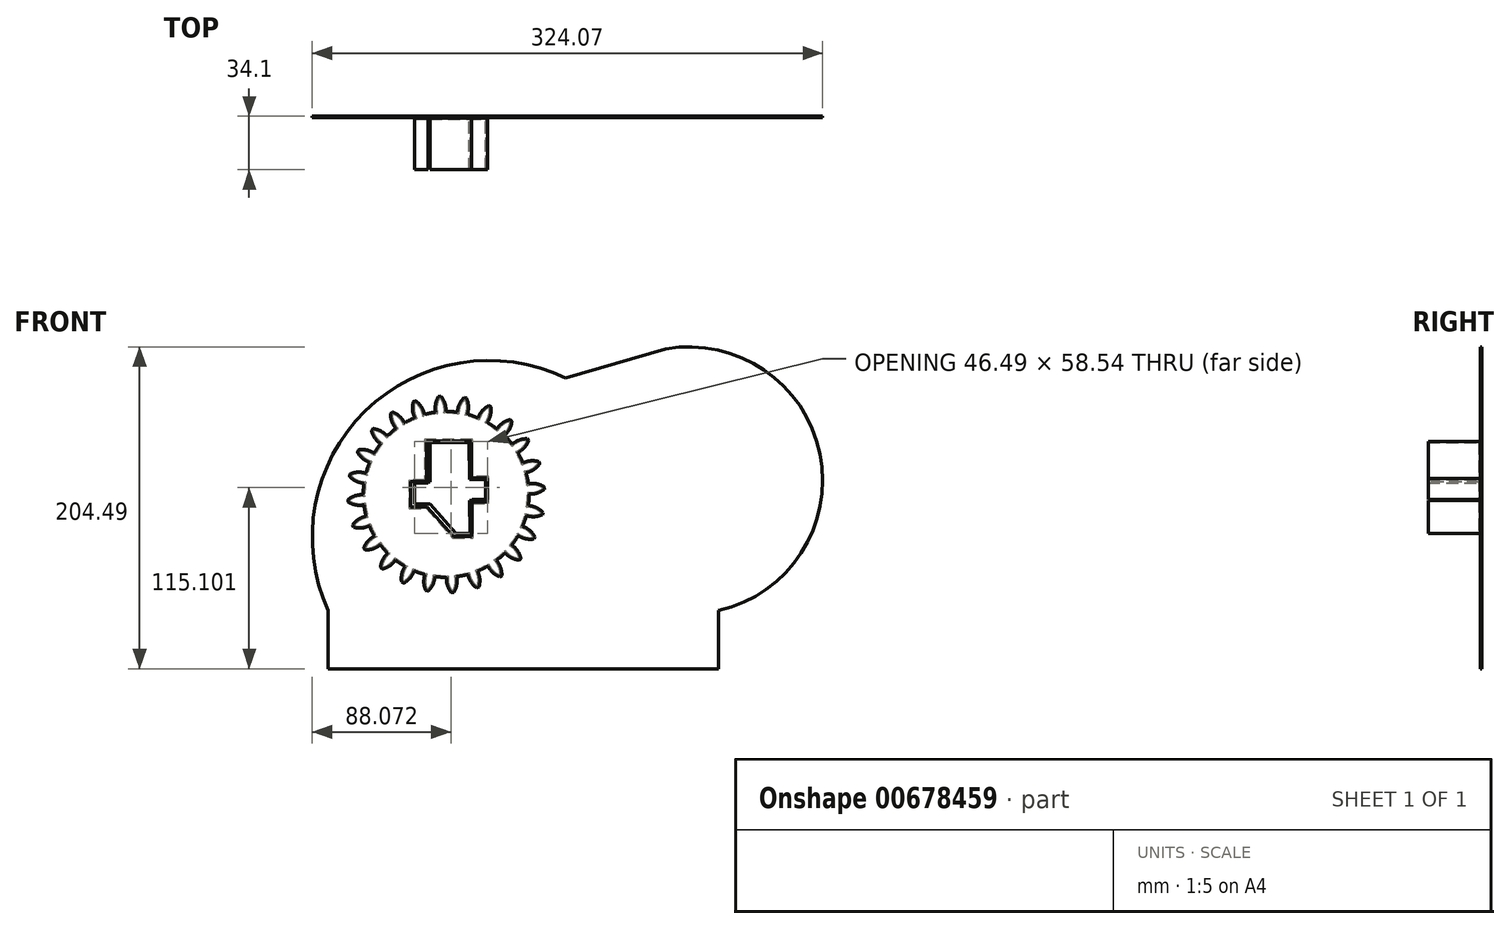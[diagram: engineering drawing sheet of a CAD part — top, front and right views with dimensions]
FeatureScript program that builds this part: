
annotation { "Feature Type Name" : "Feature", "Feature Type Description" : "" }
export const myFeature = defineFeature(function(context is Context, id is Id, definition is map)
    precondition{}
    {
        {
            var Q0;
            Q0=qCreatedBy(makeId("Front.planeOp"),FACE);
            var sketch = newSketch(context, id + "F0", { "sketchPlane" : qUnion([Q0])});
            skCircle(sketch, "E0", {"center": v(0, 0) * mm, "radius": 53.72 * mm});
            skCircle(sketch, "E1", {"center": v(0, 0) * mm, "radius": 63.5 * mm, "construction": true});
            skCircle(sketch, "E2", {"center": v(0, 0) * mm, "radius": 58.67 * mm, "construction": true});
            skLineSegment(sketch, "E3", {"start": v(0, 0) * mm, "end": v(0, 121.01) * mm, "construction": true});
            skLineSegment(sketch, "E4", {"start": v(0, 0) * mm, "end": v(-7.93, 121.01) * mm, "construction": true});
            skLineSegment(sketch, "E5", {"start": v(0, 58.67) * mm, "end": v(-96.86, 58.67) * mm, "construction": true});
            skLineSegment(sketch, "E6", {"start": v(0, 58.67) * mm, "end": v(-98.4, 22.86) * mm, "construction": true});
            skCircle(sketch, "E7", {"center": v(0, 0) * mm, "radius": 55.14 * mm, "construction": true});
            skCircle(sketch, "E8", {"center": v(0, 58.67) * mm, "radius": 14.6 * mm, "construction": true});
            skCircle(sketch, "E9", {"center": v(-13.72, 53.68) * mm, "radius": 14.6 * mm, "construction": true});
            skArc(sketch, "E10", {"start": v(0, 58.67) * mm, "mid": v(-1.21, 61.19) * mm, "end": v(-2.86, 63.44) * mm});
            skArc(sketch, "E11", {"start": v(0.8, 55.13) * mm, "mid": v(0.5, 56.92) * mm, "end": v(0, 58.67) * mm});
            skArc(sketch, "E12", {"start": v(0.88, 53.71) * mm, "mid": v(0.64, 56.23) * mm, "end": v(0, 58.67) * mm});
            skArc(sketch, "E13.MirrorCS", {"start": v(-7.88, 53.14) * mm, "mid": v(-7.98, 55.66) * mm, "end": v(-7.66, 58.17) * mm});
            skArc(sketch, "E14.MirrorCS", {"start": v(-7.66, 58.17) * mm, "mid": v(-6.79, 60.82) * mm, "end": v(-5.45, 63.27) * mm});
            skLineSegment(sketch, "E15", {"start": v(-5.45, 63.27) * mm, "end": v(-2.86, 63.44) * mm});
            skLineSegment(sketch, "E16", {"start": v(-11.56, -6.88) * mm, "end": v(-21.56, -6.88) * mm});
            skLineSegment(sketch, "E17", {"start": v(-21.56, -6.88) * mm, "end": v(-21.56, 7.27) * mm});
            skLineSegment(sketch, "E18", {"start": v(-21.56, 7.27) * mm, "end": v(-11.56, 7.27) * mm});
            skLineSegment(sketch, "E19", {"start": v(-11.56, 7.27) * mm, "end": v(-11.56, 32.9) * mm});
            skLineSegment(sketch, "E20", {"start": v(-11.56, 32.9) * mm, "end": v(14.67, 32.9) * mm});
            skLineSegment(sketch, "E21", {"start": v(14.67, 32.9) * mm, "end": v(14.72, 9.39) * mm});
            skLineSegment(sketch, "E22", {"start": v(14.72, 9.39) * mm, "end": v(24.9, 9.41) * mm});
            skLineSegment(sketch, "E23", {"start": v(24.9, 9.41) * mm, "end": v(24.93, -3.87) * mm});
            skLineSegment(sketch, "E24", {"start": v(24.93, -3.87) * mm, "end": v(14.93, -3.9) * mm});
            skLineSegment(sketch, "E25", {"start": v(14.93, -3.9) * mm, "end": v(15.04, -25.59) * mm});
            skLineSegment(sketch, "E26", {"start": v(15.04, -25.59) * mm, "end": v(5.04, -25.64) * mm});
            skLineSegment(sketch, "E27", {"start": v(5.04, -25.64) * mm, "end": v(-11.56, -6.88) * mm});
            skCircle(sketch, "E28", {"center": v(0, 0) * mm, "radius": 43.91 * mm});
            skSolve(sketch);
        }
        {
            var Q0;
            Q0=makeQuery(id+"F0.imprint","IMPRINT",FACE,{"disambiguationData":[TD([[makeQuery(id+"F0.imprint","IMPRINT",EDGE,{"derivedFrom":sQuery(id+"F0.wireOp",EDGE,"E28")}),-1.0]])]});
            var Q1;
            {var subQ5=sQuery(id+"F0.wireOp",EDGE,"E10");Q1=makeQuery(id+"F0.imprint","IMPRINT",FACE,{"disambiguationData":[TD([[makeQuery(id+"F0.imprint","IMPRINT",EDGE,{"derivedFrom":subQ5}),1.0]])]});}
            extrude(context, id + "F1", {"entities" : qUnion([Q0, Q1]), "depth" : 25 * mm, "offsetDistance" : 25 * mm});
        }
        {
            var Q0;
            Q0=makeQuery(id+"F1.opExtrude","SWEPT_BODY",BODY,{"disambiguationData":[OSD([sQuery(id+"F0.wireOp",EDGE,"E0"),sQuery(id+"F0.wireOp",EDGE,"E10"),sQuery(id+"F0.wireOp",EDGE,"E12"),sQuery(id+"F0.wireOp",EDGE,"E13.MirrorCS"),sQuery(id+"F0.wireOp",EDGE,"E14.MirrorCS"),sQuery(id+"F0.wireOp",EDGE,"E15")])]});
            var Q1;
            Q1=makeQuery(id+"F1.opExtrude","SWEPT_FACE",FACE,{"disambiguationData":[OSD([sQuery(id+"F0.wireOp",EDGE,"E0")])]});
            circularPattern(context, id + "F2", {"entities" : qUnion([Q0]), "axis" : qUnion([Q1]), "angle" : 360 * degree, "instanceCount" : 24, "equalSpace" : true});
        }
        {
            var Q0;
            Q0=makeQuery(id+"F0.imprint","IMPRINT",FACE,{"disambiguationData":[TD([[makeQuery(id+"F0.imprint","IMPRINT",EDGE,{"derivedFrom":sQuery(id+"F0.wireOp",EDGE,"E16")}),1.0]])]});
            extrude(context, id + "F3", {"entities" : qUnion([Q0]), "operationType" : NewBodyOperationType.ADD, "depth" : 34.1 * mm, "offsetDistance" : 25 * mm});
        }
        {
            var Q0;
            {var subQ0=sQuery(id+"F0.wireOp",EDGE,"E28");var subQ1=makeQuery(id+"F1.opExtrude","CAP_FACE",FACE,{"disambiguationData":[OSD([sQuery(id+"F0.wireOp",EDGE,"E0"),sQuery(id+"F0.wireOp",EDGE,"E10"),sQuery(id+"F0.wireOp",EDGE,"E11"),sQuery(id+"F0.wireOp",EDGE,"E12"),sQuery(id+"F0.wireOp",EDGE,"E13.MirrorCS"),sQuery(id+"F0.wireOp",EDGE,"E14.MirrorCS"),sQuery(id+"F0.wireOp",EDGE,"E15"),subQ0])],"isStart":true});Q0=makeQuery(id+"F3.boolean.opBoolean","MERGE",FACE,{"derivedFrom":[subQ1,makeQuery(id+"F2.opPattern","COPY",FACE,{"derivedFrom":subQ1,"instanceName":"1"}),makeQuery(id+"F2.opPattern","COPY",FACE,{"derivedFrom":subQ1,"instanceName":"2"}),makeQuery(id+"F2.opPattern","COPY",FACE,{"derivedFrom":subQ1,"instanceName":"3"}),makeQuery(id+"F2.opPattern","COPY",FACE,{"derivedFrom":subQ1,"instanceName":"4"}),makeQuery(id+"F2.opPattern","COPY",FACE,{"derivedFrom":subQ1,"instanceName":"5"}),makeQuery(id+"F2.opPattern","COPY",FACE,{"derivedFrom":subQ1,"instanceName":"6"}),makeQuery(id+"F2.opPattern","COPY",FACE,{"derivedFrom":subQ1,"instanceName":"7"}),makeQuery(id+"F2.opPattern","COPY",FACE,{"derivedFrom":subQ1,"instanceName":"8"}),makeQuery(id+"F2.opPattern","COPY",FACE,{"derivedFrom":subQ1,"instanceName":"9"}),makeQuery(id+"F2.opPattern","COPY",FACE,{"derivedFrom":subQ1,"instanceName":"10"}),makeQuery(id+"F2.opPattern","COPY",FACE,{"derivedFrom":subQ1,"instanceName":"11"}),makeQuery(id+"F2.opPattern","COPY",FACE,{"derivedFrom":subQ1,"instanceName":"12"}),makeQuery(id+"F2.opPattern","COPY",FACE,{"derivedFrom":subQ1,"instanceName":"13"}),makeQuery(id+"F2.opPattern","COPY",FACE,{"derivedFrom":subQ1,"instanceName":"14"}),makeQuery(id+"F2.opPattern","COPY",FACE,{"derivedFrom":subQ1,"instanceName":"15"}),makeQuery(id+"F2.opPattern","COPY",FACE,{"derivedFrom":subQ1,"instanceName":"16"}),makeQuery(id+"F2.opPattern","COPY",FACE,{"derivedFrom":subQ1,"instanceName":"17"}),makeQuery(id+"F2.opPattern","COPY",FACE,{"derivedFrom":subQ1,"instanceName":"18"}),makeQuery(id+"F2.opPattern","COPY",FACE,{"derivedFrom":subQ1,"instanceName":"19"}),makeQuery(id+"F2.opPattern","COPY",FACE,{"derivedFrom":subQ1,"instanceName":"20"}),makeQuery(id+"F2.opPattern","COPY",FACE,{"derivedFrom":subQ1,"instanceName":"21"}),makeQuery(id+"F2.opPattern","COPY",FACE,{"derivedFrom":subQ1,"instanceName":"22"}),makeQuery(id+"F2.opPattern","COPY",FACE,{"derivedFrom":subQ1,"instanceName":"23"}),makeQuery(id+"F3.opExtrude","CAP_FACE",FACE,{"disambiguationData":[OSD([sQuery(id+"F0.wireOp",EDGE,"E16"),sQuery(id+"F0.wireOp",EDGE,"E17"),sQuery(id+"F0.wireOp",EDGE,"E18"),sQuery(id+"F0.wireOp",EDGE,"E19"),sQuery(id+"F0.wireOp",EDGE,"E20"),sQuery(id+"F0.wireOp",EDGE,"E21"),sQuery(id+"F0.wireOp",EDGE,"E22"),sQuery(id+"F0.wireOp",EDGE,"E23"),sQuery(id+"F0.wireOp",EDGE,"E24"),sQuery(id+"F0.wireOp",EDGE,"E25"),sQuery(id+"F0.wireOp",EDGE,"E26"),sQuery(id+"F0.wireOp",EDGE,"E27"),subQ0])],"isStart":true})]});}
            var Q1;
            {var subQ0=makeQuery(id+"F1.opExtrude","CAP_FACE",FACE,{"disambiguationData":[OSD([sQuery(id+"F0.wireOp",EDGE,"E0"),sQuery(id+"F0.wireOp",EDGE,"E10"),sQuery(id+"F0.wireOp",EDGE,"E11"),sQuery(id+"F0.wireOp",EDGE,"E12"),sQuery(id+"F0.wireOp",EDGE,"E13.MirrorCS"),sQuery(id+"F0.wireOp",EDGE,"E14.MirrorCS"),sQuery(id+"F0.wireOp",EDGE,"E15"),sQuery(id+"F0.wireOp",EDGE,"E28")])],"isStart":false});Q1=makeQuery(id+"F3.boolean.opBoolean","MERGE",FACE,{"derivedFrom":[subQ0,makeQuery(id+"F2.opPattern","COPY",FACE,{"derivedFrom":subQ0,"instanceName":"1"}),makeQuery(id+"F2.opPattern","COPY",FACE,{"derivedFrom":subQ0,"instanceName":"2"}),makeQuery(id+"F2.opPattern","COPY",FACE,{"derivedFrom":subQ0,"instanceName":"3"}),makeQuery(id+"F2.opPattern","COPY",FACE,{"derivedFrom":subQ0,"instanceName":"4"}),makeQuery(id+"F2.opPattern","COPY",FACE,{"derivedFrom":subQ0,"instanceName":"5"}),makeQuery(id+"F2.opPattern","COPY",FACE,{"derivedFrom":subQ0,"instanceName":"6"}),makeQuery(id+"F2.opPattern","COPY",FACE,{"derivedFrom":subQ0,"instanceName":"7"}),makeQuery(id+"F2.opPattern","COPY",FACE,{"derivedFrom":subQ0,"instanceName":"8"}),makeQuery(id+"F2.opPattern","COPY",FACE,{"derivedFrom":subQ0,"instanceName":"9"}),makeQuery(id+"F2.opPattern","COPY",FACE,{"derivedFrom":subQ0,"instanceName":"10"}),makeQuery(id+"F2.opPattern","COPY",FACE,{"derivedFrom":subQ0,"instanceName":"11"}),makeQuery(id+"F2.opPattern","COPY",FACE,{"derivedFrom":subQ0,"instanceName":"12"}),makeQuery(id+"F2.opPattern","COPY",FACE,{"derivedFrom":subQ0,"instanceName":"13"}),makeQuery(id+"F2.opPattern","COPY",FACE,{"derivedFrom":subQ0,"instanceName":"14"}),makeQuery(id+"F2.opPattern","COPY",FACE,{"derivedFrom":subQ0,"instanceName":"15"}),makeQuery(id+"F2.opPattern","COPY",FACE,{"derivedFrom":subQ0,"instanceName":"16"}),makeQuery(id+"F2.opPattern","COPY",FACE,{"derivedFrom":subQ0,"instanceName":"17"}),makeQuery(id+"F2.opPattern","COPY",FACE,{"derivedFrom":subQ0,"instanceName":"18"}),makeQuery(id+"F2.opPattern","COPY",FACE,{"derivedFrom":subQ0,"instanceName":"19"}),makeQuery(id+"F2.opPattern","COPY",FACE,{"derivedFrom":subQ0,"instanceName":"20"}),makeQuery(id+"F2.opPattern","COPY",FACE,{"derivedFrom":subQ0,"instanceName":"21"}),makeQuery(id+"F2.opPattern","COPY",FACE,{"derivedFrom":subQ0,"instanceName":"22"}),makeQuery(id+"F2.opPattern","COPY",FACE,{"derivedFrom":subQ0,"instanceName":"23"})]});}
            chamfer(context, id + "F4", {"entities" : qUnion([Q0, Q1]), "width" : 2 * mm, "tangentPropagation" : true});
        }
        {
            var Q0;
            Q0=qCreatedBy(makeId("Front.planeOp"),FACE);
            var sketch = newSketch(context, id + "F5", { "sketchPlane" : qUnion([Q0])});
            skLineSegment(sketch, "E29", {"start": v(-74.86, -73.82) * mm, "end": v(-74.86, -110.79) * mm});
            skLineSegment(sketch, "E30", {"start": v(-74.86, -110.79) * mm, "end": v(173, -110.79) * mm});
            skLineSegment(sketch, "E31", {"start": v(173, -110.79) * mm, "end": v(173, -73.82) * mm});
            skArc(sketch, "E32", {"start": v(75.87, 73.9) * mm, "mid": v(-51.34, 52.95) * mm, "end": v(-74.86, -73.82) * mm});
            skLineSegment(sketch, "E33", {"start": v(75.87, 73.9) * mm, "end": v(139.38, 92.39) * mm});
            skArc(sketch, "E34", {"start": v(173, -73.82) * mm, "mid": v(237.38, 25.7) * mm, "end": v(139.38, 92.39) * mm});
            skLineSegment(sketch, "E35", {"start": v(-10.18, -6.2) * mm, "end": v(-20.18, -6.2) * mm});
            skLineSegment(sketch, "E36", {"start": v(-20.18, -6.2) * mm, "end": v(-20.18, 7.95) * mm});
            skLineSegment(sketch, "E37", {"start": v(-20.18, 7.95) * mm, "end": v(-10.18, 7.95) * mm});
            skLineSegment(sketch, "E38", {"start": v(-10.18, 7.95) * mm, "end": v(-10.18, 33.58) * mm});
            skLineSegment(sketch, "E39", {"start": v(-10.18, 33.58) * mm, "end": v(16.05, 33.58) * mm});
            skLineSegment(sketch, "E40", {"start": v(16.05, 33.58) * mm, "end": v(16.1, 10.07) * mm});
            skLineSegment(sketch, "E41", {"start": v(16.1, 10.07) * mm, "end": v(26.28, 10.1) * mm});
            skLineSegment(sketch, "E42", {"start": v(26.28, 10.1) * mm, "end": v(26.3, -3.19) * mm});
            skLineSegment(sketch, "E43", {"start": v(26.3, -3.19) * mm, "end": v(16.3, -3.2) * mm});
            skLineSegment(sketch, "E44", {"start": v(16.3, -3.2) * mm, "end": v(16.42, -24.9) * mm});
            skLineSegment(sketch, "E45", {"start": v(16.42, -24.9) * mm, "end": v(6.42, -24.96) * mm});
            skLineSegment(sketch, "E46", {"start": v(6.42, -24.96) * mm, "end": v(-10.18, -6.2) * mm});
            skSolve(sketch);
        }
        {
            var Q0;
            Q0 = qSketchRegion(id + "F5", true);
            extrude(context, id + "F6", {"entities" : qUnion([Q0]), "depth" : 50 * mm, "offsetDistance" : 25 * mm});
        }
        {
            var Q0;
            Q0=makeQuery(id+"F6.opExtrude","CAP_FACE",FACE,{"disambiguationData":[OSD([sQuery(id+"F5.wireOp",EDGE,"E29"),sQuery(id+"F5.wireOp",EDGE,"E30"),sQuery(id+"F5.wireOp",EDGE,"E31"),sQuery(id+"F5.wireOp",EDGE,"E32"),sQuery(id+"F5.wireOp",EDGE,"E33"),sQuery(id+"F5.wireOp",EDGE,"E34"),sQuery(id+"F5.wireOp",EDGE,"E35"),sQuery(id+"F5.wireOp",EDGE,"E36"),sQuery(id+"F5.wireOp",EDGE,"E37"),sQuery(id+"F5.wireOp",EDGE,"E38"),sQuery(id+"F5.wireOp",EDGE,"E39"),sQuery(id+"F5.wireOp",EDGE,"E40"),sQuery(id+"F5.wireOp",EDGE,"E41"),sQuery(id+"F5.wireOp",EDGE,"E42"),sQuery(id+"F5.wireOp",EDGE,"E43"),sQuery(id+"F5.wireOp",EDGE,"E44"),sQuery(id+"F5.wireOp",EDGE,"E45"),sQuery(id+"F5.wireOp",EDGE,"E46")])],"isStart":false});
            extrude(context, id + "F7", {"entities" : qUnion([Q0]), "operationType" : NewBodyOperationType.REMOVE, "oppositeDirection" : true, "depth" : 49 * mm, "offsetDistance" : 25 * mm});
        }
    });
